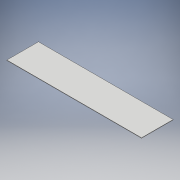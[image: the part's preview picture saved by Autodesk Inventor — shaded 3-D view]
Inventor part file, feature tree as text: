
AUTODESK INVENTOR PART (.ipt)
format: ipt  version: 2018 (Build 220112000, 112)  size: 91,648 bytes
history: native  units: mm
features: other x1, extrude x1, sketch x1
ambient origin geometry x8: Origin, YZ Plane, XZ Plane, XY Plane, X Axis, Y Axis, Z Axis, Center Point
bodies: Body1 (feature_tree)
feature tree (3):
  other  "ソリッド1"
  extrude  "押し出し1"  Depth=1280.0mm
  sketch  "スケッチ1"
